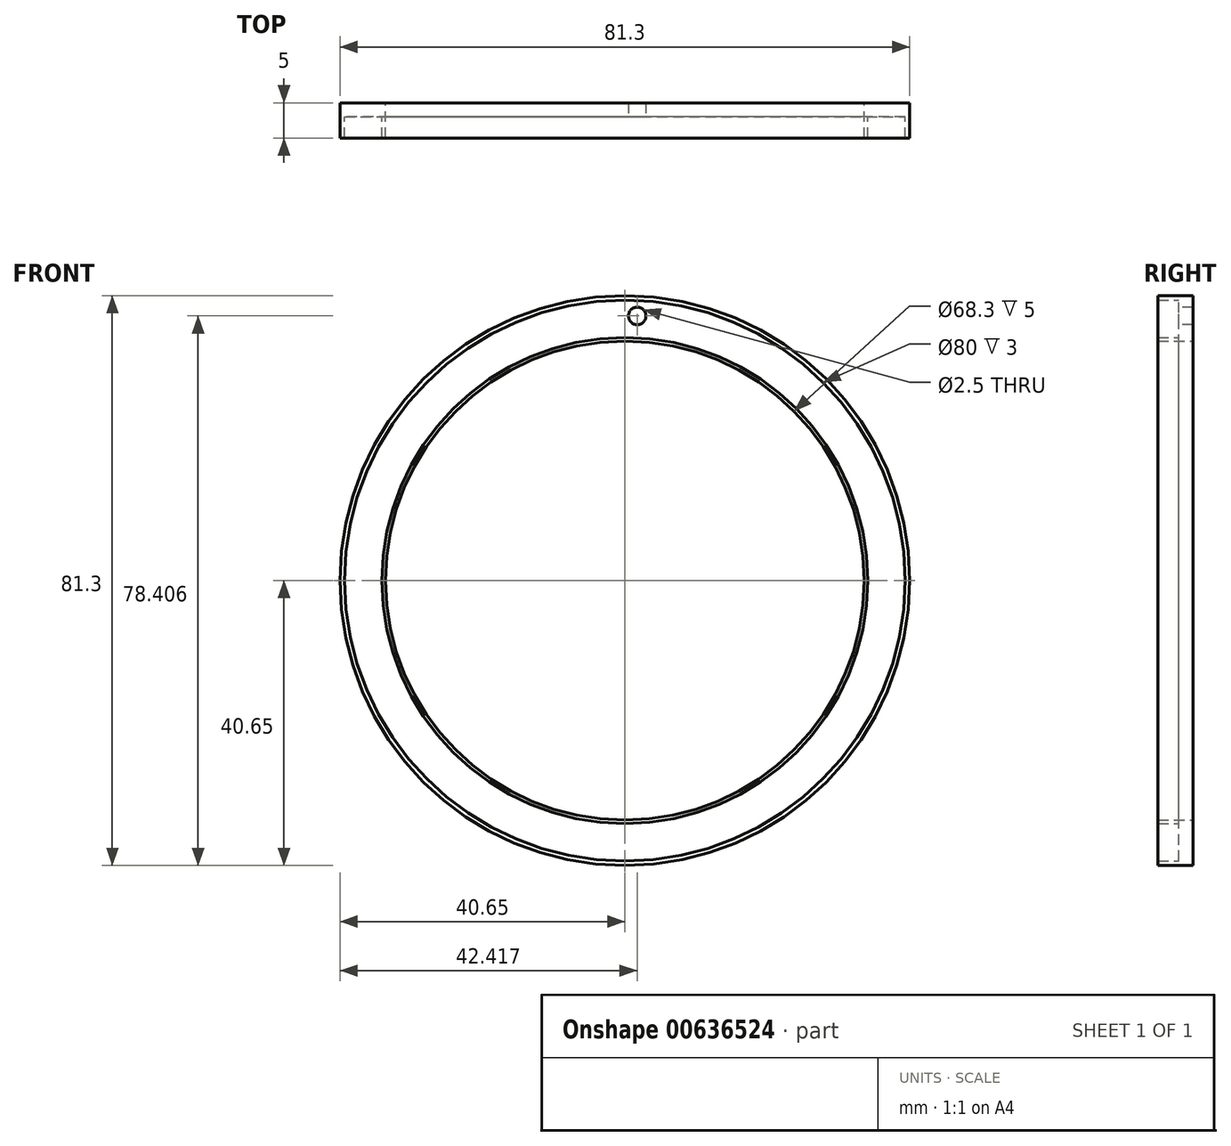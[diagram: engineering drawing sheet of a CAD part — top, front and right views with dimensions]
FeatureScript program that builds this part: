
annotation { "Feature Type Name" : "Feature", "Feature Type Description" : "" }
export const myFeature = defineFeature(function(context is Context, id is Id, definition is map)
    precondition{}
    {
        {
            var Q0;
            Q0=qCreatedBy(makeId("Front.planeOp"),FACE);
            var sketch = newSketch(context, id + "F0", { "sketchPlane" : qUnion([Q0])});
            skCircle(sketch, "E0", {"center": v(0, 0) * mm, "radius": 34.15 * mm});
            skCircle(sketch, "E1", {"center": v(0, 0) * mm, "radius": 40.65 * mm});
            skSolve(sketch);
        }
        {
            var Q0;
            Q0 = qSketchRegion(id + "F0", true);
            extrude(context, id + "F1", {"entities" : qUnion([Q0]), "depth" : 2 * mm, "offsetDistance" : 25 * mm});
        }
        {
            var Q0;
            Q0=makeQuery(id+"F1.opExtrude","CAP_FACE",FACE,{"disambiguationData":[OSD([sQuery(id+"F0.wireOp",EDGE,"E0"),sQuery(id+"F0.wireOp",EDGE,"E1")])],"isStart":false});
            var sketch = newSketch(context, id + "F2", { "sketchPlane" : qUnion([Q0])});
            skCircle(sketch, "E2", {"center": v(0, 0) * mm, "radius": 40 * mm});
            skSolve(sketch);
        }
        {
            var Q0;
            Q0=makeQuery(id+"F2.imprint","IMPRINT",FACE,{"disambiguationData":[TD([[makeQuery(id+"F2.imprint","IMPRINT",EDGE,{"derivedFrom":sQuery(id+"F2.wireOp",EDGE,"E2")}),-1.0]])]});
            extrude(context, id + "F3", {"entities" : qUnion([Q0]), "operationType" : NewBodyOperationType.ADD, "depth" : 3 * mm, "offsetDistance" : 25 * mm});
        }
        {
            var Q0;
            Q0=makeQuery(id+"F1.opExtrude","CAP_FACE",FACE,{"disambiguationData":[OSD([sQuery(id+"F0.wireOp",EDGE,"E0"),sQuery(id+"F0.wireOp",EDGE,"E1")])],"isStart":false});
            var sketch = newSketch(context, id + "F4", { "sketchPlane" : qUnion([Q0])});
            skCircle(sketch, "E3", {"center": v(0, 0) * mm, "radius": 34.65 * mm});
            skSolve(sketch);
        }
        {
            var Q0;
            Q0=makeQuery(id+"F4.imprint","IMPRINT",FACE,{"disambiguationData":[TD([[makeQuery(id+"F4.imprint","IMPRINT",EDGE,{"derivedFrom":sQuery(id+"F4.wireOp",EDGE,"E3")}),1.0]])]});
            extrude(context, id + "F5", {"entities" : qUnion([Q0]), "operationType" : NewBodyOperationType.ADD, "depth" : 3 * mm, "offsetDistance" : 25 * mm});
        }
        {
            var Q0;
            Q0=makeQuery(id+"F1.opExtrude","CAP_FACE",FACE,{"disambiguationData":[OSD([sQuery(id+"F0.wireOp",EDGE,"E0"),sQuery(id+"F0.wireOp",EDGE,"E1")])],"isStart":false});
            var sketch = newSketch(context, id + "F6", { "sketchPlane" : qUnion([Q0])});
            skCircle(sketch, "E4", {"center": v(1.77, 37.76) * mm, "radius": 1.25 * mm});
            skSolve(sketch);
        }
        {
            var Q0;
            Q0 = qSketchRegion(id + "F6", true);
            extrude(context, id + "F7", {"entities" : qUnion([Q0]), "operationType" : NewBodyOperationType.REMOVE, "oppositeDirection" : true, "depth" : 25 * mm, "offsetDistance" : 25 * mm});
        }
    });
